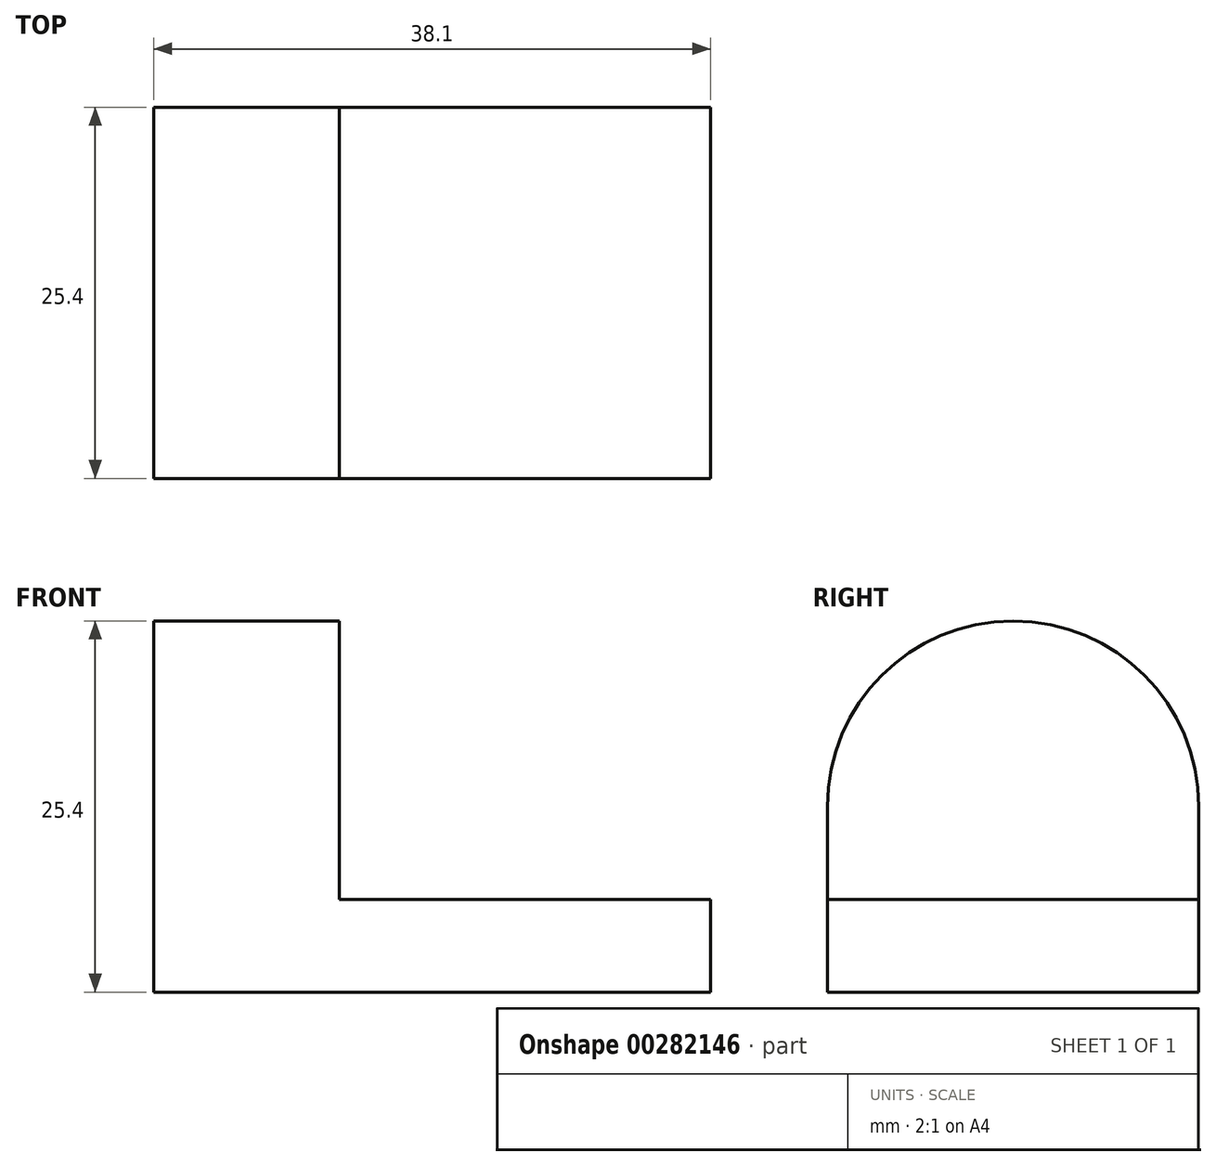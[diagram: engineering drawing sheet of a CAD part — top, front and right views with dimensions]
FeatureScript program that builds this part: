
annotation { "Feature Type Name" : "Feature", "Feature Type Description" : "" }
export const myFeature = defineFeature(function(context is Context, id is Id, definition is map)
    precondition{}
    {
        {
            var Q0;
            Q0=qCreatedBy(makeId("Right.planeOp"),FACE);
            var sketch = newSketch(context, id + "F0", { "sketchPlane" : qUnion([Q0])});
            skLineSegment(sketch, "E0.bottom", {"start": v(0, 0) * mm, "end": v(-25.4, 0) * mm});
            skLineSegment(sketch, "E0.top", {"start": v(0, 6.35) * mm, "end": v(-25.4, 6.35) * mm});
            skLineSegment(sketch, "E0.left", {"start": v(0, 0) * mm, "end": v(0, 6.35) * mm});
            skLineSegment(sketch, "E0.right", {"start": v(-25.4, 0) * mm, "end": v(-25.4, 6.35) * mm});
            skLineSegment(sketch, "E1", {"start": v(-25.4, 6.35) * mm, "end": v(-25.4, 12.7) * mm});
            skLineSegment(sketch, "E2", {"start": v(0, 6.35) * mm, "end": v(0, 12.7) * mm});
            skArc(sketch, "E3", {"start": v(0, 12.7) * mm, "mid": v(-12.7, 25.4) * mm, "end": v(-25.4, 12.7) * mm});
            skSolve(sketch);
        }
        {
            var Q0;
            Q0=makeQuery(id+"F0.imprint","IMPRINT",FACE,{"disambiguationData":[TD([[makeQuery(id+"F0.imprint","IMPRINT",EDGE,{"derivedFrom":sQuery(id+"F0.wireOp",EDGE,"E0.bottom")}),-1.0]])]});
            extrude(context, id + "F1", {"entities" : qUnion([Q0]), "depth" : 38.1 * mm});
        }
        {
            var Q0;
            Q0=makeQuery(id+"F0.imprint","IMPRINT",FACE,{"disambiguationData":[TD([[makeQuery(id+"F0.imprint","IMPRINT",EDGE,{"derivedFrom":sQuery(id+"F0.wireOp",EDGE,"E0.top")}),-1.0]])]});
            extrude(context, id + "F2", {"entities" : qUnion([Q0]), "operationType" : NewBodyOperationType.ADD, "depth" : 12.7 * mm});
        }
    });
